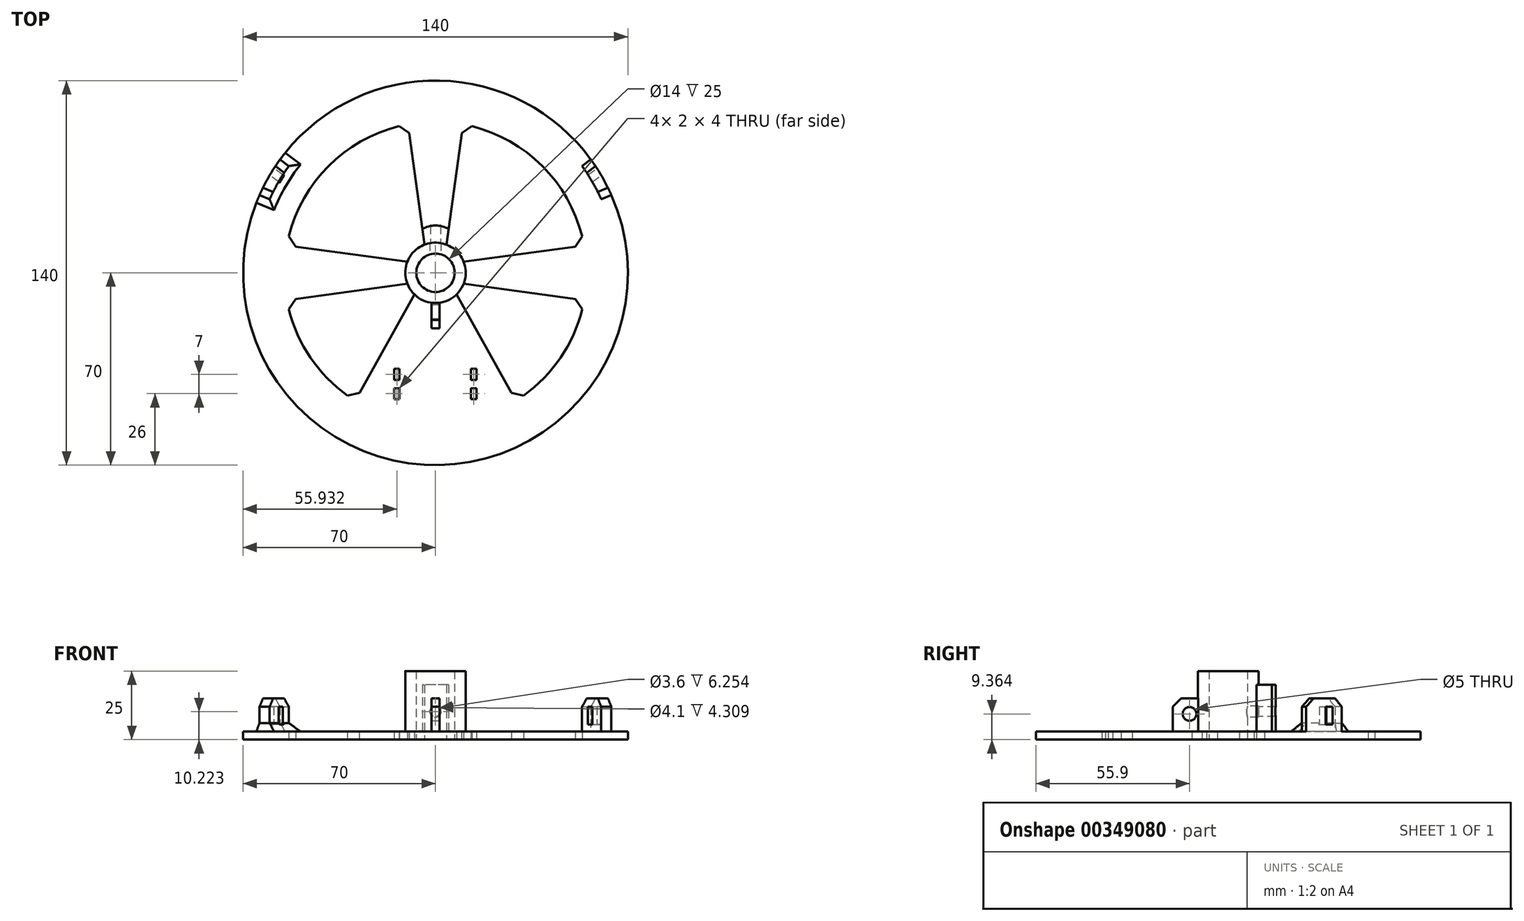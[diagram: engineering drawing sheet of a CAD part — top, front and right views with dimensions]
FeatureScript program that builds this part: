
annotation { "Feature Type Name" : "Feature", "Feature Type Description" : "" }
export const myFeature = defineFeature(function(context is Context, id is Id, definition is map)
    precondition{}
    {
        {
            var Q0;
            Q0=qCreatedBy(makeId("Top.planeOp"),FACE);
            var sketch = newSketch(context, id + "F0", { "sketchPlane" : qUnion([Q0])});
            skLineSegment(sketch, "E0", {"start": v(0, 0) * mm, "end": v(69.9, 40.35) * mm, "construction": true});
            skLineSegment(sketch, "E1", {"start": v(0, 0) * mm, "end": v(-75.47, 43.58) * mm, "construction": true});
            skLineSegment(sketch, "E2", {"start": v(0, 0) * mm, "end": v(0, -74.2) * mm, "construction": true});
            skArc(sketch, "E3", {"start": v(-56.52, 41.3) * mm, "mid": v(-60.62, 35) * mm, "end": v(-64.02, 28.3) * mm});
            skArc(sketch, "E4", {"start": v(-64.02, 28.3) * mm, "mid": v(60.62, -35) * mm, "end": v(-56.52, 41.3) * mm});
            skArc(sketch, "E5", {"start": v(-53.34, 38.88) * mm, "mid": v(-57.16, 33) * mm, "end": v(-60.34, 26.75) * mm});
            skLineSegment(sketch, "E6", {"start": v(-64.02, 28.3) * mm, "end": v(-60.34, 26.75) * mm});
            skLineSegment(sketch, "E7", {"start": v(-53.34, 38.88) * mm, "end": v(-56.52, 41.3) * mm});
            skCircle(sketch, "E8", {"center": v(0, 0) * mm, "radius": 7 * mm});
            skCircle(sketch, "E9", {"center": v(0, 0) * mm, "radius": 11 * mm});
            skArc(sketch, "E10.2.0", {"start": v(60.34, 26.75) * mm, "mid": v(57.16, 33) * mm, "end": v(53.34, 38.88) * mm});
            skArc(sketch, "E10.2.1", {"start": v(64.02, 28.3) * mm, "mid": v(60.62, 35) * mm, "end": v(56.52, 41.3) * mm});
            skLineSegment(sketch, "E10.2.2", {"start": v(56.52, 41.3) * mm, "end": v(53.34, 38.88) * mm});
            skLineSegment(sketch, "E10.2.3", {"start": v(60.34, 26.75) * mm, "end": v(64.02, 28.3) * mm});
            skCircle(sketch, "E11", {"center": v(0, 0) * mm, "radius": 55 * mm});
            skLineSegment(sketch, "E12", {"start": v(0, 71.1) * mm, "end": v(0, -3.57) * mm, "construction": true});
            skLineSegment(sketch, "E13", {"start": v(-10, 54.08) * mm, "end": v(-4, 10.25) * mm});
            skLineSegment(sketch, "E14", {"start": v(10, 54.08) * mm, "end": v(4, 10.25) * mm});
            skLineSegment(sketch, "E15.1.0", {"start": v(-54.08, 10) * mm, "end": v(-10.25, 4) * mm});
            skLineSegment(sketch, "E15.1.1", {"start": v(-54.08, -10) * mm, "end": v(-10.25, -4) * mm});
            skLineSegment(sketch, "E15.3.0", {"start": v(54.08, -10) * mm, "end": v(10.25, -4) * mm});
            skLineSegment(sketch, "E15.3.1", {"start": v(54.08, 10) * mm, "end": v(10.25, 4) * mm});
            skArc(sketch, "E16", {"start": v(4.77, 15.87) * mm, "mid": v(0, 17.25) * mm, "end": v(-4.77, 15.87) * mm});
            skLineSegment(sketch, "E17", {"start": v(-1.5, -10.9) * mm, "end": v(-1.5, -20.16) * mm});
            skLineSegment(sketch, "E18", {"start": v(-1.5, -20.16) * mm, "end": v(1.5, -20.16) * mm});
            skLineSegment(sketch, "E19", {"start": v(1.5, -20.16) * mm, "end": v(1.5, -10.9) * mm});
            skLineSegment(sketch, "E20.bottom", {"start": v(-15.07, -35) * mm, "end": v(-13.07, -35) * mm});
            skLineSegment(sketch, "E20.top", {"start": v(-15.07, -39) * mm, "end": v(-13.07, -39) * mm});
            skLineSegment(sketch, "E20.left", {"start": v(-15.07, -35) * mm, "end": v(-15.07, -39) * mm});
            skLineSegment(sketch, "E20.right", {"start": v(-13.07, -35) * mm, "end": v(-13.07, -39) * mm});
            skLineSegment(sketch, "E21.bottom", {"start": v(12.93, -35) * mm, "end": v(14.93, -35) * mm});
            skLineSegment(sketch, "E21.top", {"start": v(12.93, -39) * mm, "end": v(14.93, -39) * mm});
            skLineSegment(sketch, "E21.left", {"start": v(12.93, -35) * mm, "end": v(12.93, -39) * mm});
            skLineSegment(sketch, "E21.right", {"start": v(14.93, -35) * mm, "end": v(14.93, -39) * mm});
            skLineSegment(sketch, "E22", {"start": v(-18.61, -37) * mm, "end": v(20.4, -37) * mm, "construction": true});
            skLineSegment(sketch, "E23.bottom", {"start": v(-15.07, -42) * mm, "end": v(-13.07, -42) * mm});
            skLineSegment(sketch, "E23.top", {"start": v(-15.07, -46) * mm, "end": v(-13.07, -46) * mm});
            skLineSegment(sketch, "E23.left", {"start": v(-15.07, -42) * mm, "end": v(-15.07, -46) * mm});
            skLineSegment(sketch, "E23.right", {"start": v(-13.07, -42) * mm, "end": v(-13.07, -46) * mm});
            skLineSegment(sketch, "E24.bottom", {"start": v(12.93, -42) * mm, "end": v(14.93, -42) * mm});
            skLineSegment(sketch, "E24.top", {"start": v(12.93, -46) * mm, "end": v(14.93, -46) * mm});
            skLineSegment(sketch, "E24.left", {"start": v(12.93, -42) * mm, "end": v(12.93, -46) * mm});
            skLineSegment(sketch, "E24.right", {"start": v(14.93, -42) * mm, "end": v(14.93, -46) * mm});
            skLineSegment(sketch, "E25", {"start": v(-18.62, -44) * mm, "end": v(19.75, -44) * mm, "construction": true});
            skLineSegment(sketch, "E26", {"start": v(-14.07, -36.98) * mm, "end": v(-14.07, -57.94) * mm, "construction": true});
            skPoint(sketch, "E26.startSnap0", {"position": v(-14.07, -35) * mm});
            skLineSegment(sketch, "E27", {"start": v(-7.65, -7.9) * mm, "end": v(-29.25, -46.57) * mm});
            skLineSegment(sketch, "E28", {"start": v(7.65, -7.9) * mm, "end": v(29.25, -46.57) * mm});
            skSolve(sketch);
        }
        {
            var Q0;
            Q0=makeQuery(id+"F0.imprint","IMPRINT",FACE,{"disambiguationData":[TD([[makeQuery(id+"F0.imprint","IMPRINT",EDGE,{"derivedFrom":sQuery(id+"F0.wireOp",EDGE,"E3")}),1.0]])]});
            var Q1;
            Q1=makeQuery(id+"F0.imprint","IMPRINT",FACE,{"disambiguationData":[TD([[makeQuery(id+"F0.imprint","IMPRINT",EDGE,{"derivedFrom":sQuery(id+"F0.wireOp",EDGE,"E5")}),1.0]])]});
            var Q2;
            Q2=makeQuery(id+"F0.imprint","IMPRINT",FACE,{"disambiguationData":[TD([[makeQuery(id+"F0.imprint","IMPRINT",EDGE,{"derivedFrom":sQuery(id+"F0.wireOp",EDGE,"E4")}),1.0]])]});
            var Q3;
            {var subQ0=sQuery(id+"F0.wireOp",EDGE,"E15.1.0");Q3=makeQuery(id+"F0.imprint","IMPRINT",FACE,{"disambiguationData":[TD([[makeQuery(id+"F0.imprint","IMPRINT",EDGE,{"derivedFrom":subQ0}),-1.0]])]});}
            var Q4;
            {var subQ0=sQuery(id+"F0.wireOp",EDGE,"E13");Q4=makeQuery(id+"F0.imprint","IMPRINT",FACE,{"disambiguationData":[TD([[makeQuery(id+"F0.imprint","IMPRINT",EDGE,{"derivedFrom":subQ0}),1.0]])]});}
            var Q5;
            {var subQ0=sQuery(id+"F0.wireOp",EDGE,"E15.3.0");Q5=makeQuery(id+"F0.imprint","IMPRINT",FACE,{"disambiguationData":[TD([[makeQuery(id+"F0.imprint","IMPRINT",EDGE,{"derivedFrom":subQ0}),-1.0]])]});}
            var Q6;
            {var subQ0=sQuery(id+"F0.wireOp",EDGE,"E15.2.0");Q6=makeQuery(id+"F0.imprint","IMPRINT",FACE,{"disambiguationData":[TD([[makeQuery(id+"F0.imprint","IMPRINT",EDGE,{"derivedFrom":subQ0}),-1.0]])]});}
            var Q7;
            Q7=makeQuery(id+"F0.imprint","IMPRINT",FACE,{"disambiguationData":[TD([[makeQuery(id+"F0.imprint","IMPRINT",EDGE,{"derivedFrom":sQuery(id+"F0.wireOp",EDGE,"DxC1QGky-HRrN-gzPb-Pb88-aNf4S9f9K86J.bottom")}),1.0]])]});
            var Q8;
            {var subQ0=sQuery(id+"F0.wireOp",EDGE,"E17");Q8=makeQuery(id+"F0.imprint","IMPRINT",FACE,{"disambiguationData":[TD([[makeQuery(id+"F0.imprint","IMPRINT",EDGE,{"derivedFrom":subQ0}),-1.0]])]});}
            extrude(context, id + "F1", {"entities" : qUnion([Q0, Q1, Q2, Q3, Q4, Q5, Q6, Q7, Q8]), "depth" : 3 * mm});
        }
        {
            var Q0;
            Q0=makeQuery(id+"F0.imprint","IMPRINT",FACE,{"disambiguationData":[TD([[makeQuery(id+"F0.imprint","IMPRINT",EDGE,{"derivedFrom":sQuery(id+"F0.wireOp",EDGE,"E3")}),1.0]])]});
            var Q1;
            Q1=makeQuery(id+"F0.imprint","IMPRINT",FACE,{"disambiguationData":[TD([[makeQuery(id+"F0.imprint","IMPRINT",EDGE,{"derivedFrom":sQuery(id+"F0.wireOp",EDGE,"E10.2.0")}),-1.0]])]});
            var Q2;
            Q2=makeQuery(id+"F0.imprint","IMPRINT",FACE,{"disambiguationData":[TD([[makeQuery(id+"F0.imprint","IMPRINT",EDGE,{"derivedFrom":sQuery(id+"F0.wireOp",EDGE,"E10.1.0")}),-1.0]])]});
            var Q3;
            {var subQ0=sQuery(id+"F0.wireOp",EDGE,"E17");Q3=makeQuery(id+"F0.imprint","IMPRINT",FACE,{"disambiguationData":[TD([[makeQuery(id+"F0.imprint","IMPRINT",EDGE,{"derivedFrom":subQ0}),1.0]])]});}
            extrude(context, id + "F2", {"entities" : qUnion([Q0, Q1, Q2, Q3]), "operationType" : NewBodyOperationType.ADD, "depth" : 15 * mm});
        }
        {
            var Q0;
            Q0=qCreatedBy(makeId("Right.planeOp"),FACE);
            var sketch = newSketch(context, id + "F3", { "sketchPlane" : qUnion([Q0])});
            skLineSegment(sketch, "E29", {"start": v(0, 42.43) * mm, "end": v(0, -20.95) * mm, "construction": true});
            skSolve(sketch);
        }
        {
            var Q0;
            Q0=makeQuery(id+"F0.imprint","IMPRINT",FACE,{"disambiguationData":[TD([[makeQuery(id+"F0.imprint","IMPRINT",EDGE,{"derivedFrom":sQuery(id+"F0.wireOp",EDGE,"E8")}),-1.0]])]});
            extrude(context, id + "F4", {"entities" : qUnion([Q0]), "operationType" : NewBodyOperationType.ADD, "depth" : 25 * mm});
        }
        {
            var Q0;
            {var subQ5=sQuery(id+"F0.wireOp",EDGE,"E16");Q0=makeQuery(id+"F0.imprint","IMPRINT",FACE,{"disambiguationData":[TD([[makeQuery(id+"F0.imprint","IMPRINT",EDGE,{"derivedFrom":subQ5}),1.0]])]});}
            extrude(context, id + "F5", {"entities" : qUnion([Q0]), "operationType" : NewBodyOperationType.ADD, "depth" : 20 * mm});
        }
        {
            var Q0;
            Q0=sQuery(id+"F3.wireOp",EDGE,"E29");
            cPlane(context, id + "F6", {"entities" : qUnion([Q0]), "cplaneType" : CPlaneType.LINE_ANGLE, "offset" : 25 * mm, "angle" : 90 * degree, "width" : 150 * mm, "height" : 150 * mm});
        }
        {
            var Q0;
            Q0=qCreatedBy(id+"F6.planeOp",FACE);
            var sketch = newSketch(context, id + "F7", { "sketchPlane" : qUnion([Q0])});
            skCircle(sketch, "E30", {"center": v(0, 10.22) * mm, "radius": 1 * mm});
            skSolve(sketch);
        }
        {
            var Q0;
            Q0=sQuery(id+"F7.wireOp",VERTEX,"E30.center");
            var Q1;
            Q1=makeQuery(id+"F1.opExtrude","SWEPT_BODY",BODY,{"disambiguationData":[OSD([sQuery(id+"F0.wireOp",EDGE,"E3"),sQuery(id+"F0.wireOp",EDGE,"E4"),sQuery(id+"F0.wireOp",EDGE,"E9"),sQuery(id+"F0.wireOp",EDGE,"E10.1.0"),sQuery(id+"F0.wireOp",EDGE,"E10.1.2"),sQuery(id+"F0.wireOp",EDGE,"E10.1.3"),sQuery(id+"F0.wireOp",EDGE,"E10.2.0"),sQuery(id+"F0.wireOp",EDGE,"E10.2.2"),sQuery(id+"F0.wireOp",EDGE,"E10.2.3"),sQuery(id+"F0.wireOp",EDGE,"E11"),sQuery(id+"F0.wireOp",EDGE,"E13"),sQuery(id+"F0.wireOp",EDGE,"E14"),sQuery(id+"F0.wireOp",EDGE,"E15.1.0"),sQuery(id+"F0.wireOp",EDGE,"E15.1.1"),sQuery(id+"F0.wireOp",EDGE,"E15.3.0"),sQuery(id+"F0.wireOp",EDGE,"E15.3.1"),sQuery(id+"F0.wireOp",EDGE,"DxC1QGky-HRrN-gzPb-Pb88-aNf4S9f9K86J.bottom"),sQuery(id+"F0.wireOp",EDGE,"DxC1QGky-HRrN-gzPb-Pb88-aNf4S9f9K86J.top"),sQuery(id+"F0.wireOp",EDGE,"DxC1QGky-HRrN-gzPb-Pb88-aNf4S9f9K86J.left"),sQuery(id+"F0.wireOp",EDGE,"DxC1QGky-HRrN-gzPb-Pb88-aNf4S9f9K86J.right"),sQuery(id+"F0.wireOp",EDGE,"2d52bbff-8edd-4f97-a77e-c5ac5676539f0.MirrorCS"),sQuery(id+"F0.wireOp",EDGE,"2d52bbff-8edd-4f97-a77e-c5ac5676539f1.MirrorCS"),sQuery(id+"F0.wireOp",EDGE,"2d52bbff-8edd-4f97-a77e-c5ac5676539f3.MirrorCS"),sQuery(id+"F0.wireOp",EDGE,"2d52bbff-8edd-4f97-a77e-c5ac5676539f6.MirrorCS"),sQuery(id+"F0.wireOp",EDGE,"9be3de77-d5e6-4486-93f5-ee3b1d01e160.bottom"),sQuery(id+"F0.wireOp",EDGE,"9be3de77-d5e6-4486-93f5-ee3b1d01e160.top"),sQuery(id+"F0.wireOp",EDGE,"9be3de77-d5e6-4486-93f5-ee3b1d01e160.left"),sQuery(id+"F0.wireOp",EDGE,"9be3de77-d5e6-4486-93f5-ee3b1d01e160.right"),sQuery(id+"F0.wireOp",EDGE,"a1a42e55-1d56-4dcf-bef6-dfa0cd09f213.MirrorCS"),sQuery(id+"F0.wireOp",EDGE,"69599f0c-71d3-4e93-93c2-72b703701d98.MirrorCS"),sQuery(id+"F0.wireOp",EDGE,"1db623de-f78b-4af5-8506-0e3137d38347.MirrorCS"),sQuery(id+"F0.wireOp",EDGE,"2d571f0c-88a3-41e3-b531-1a1a6e09f5e6.MirrorCS"),sQuery(id+"F0.wireOp",EDGE,"QAUAg4Rv-rJLO-vGMV-bjQP-bpTTJf4zCCb9"),sQuery(id+"F0.wireOp",EDGE,"6e9785c6-ce13-4db9-ba87-197f2c4649aa0.MirrorCS")])]});
            hole(context, id + "F8", {"style" : HoleStyle.C_BORE, "endStyle" : HoleEndStyle.THROUGH, "oppositeDirection" : true, "holeDiameter" : 3.6 * mm, "cBoreDiameter" : 4.1 * mm, "cBoreDepth" : 11 * mm, "isTappedThrough" : true, "tappedDepth" : 12 * mm, "tapClearance" : 3, "startFromSketch" : true, "locations" : qUnion([Q0]), "scope" : qUnion([Q1])});
        }
        {
            var Q0;
            Q0=makeQuery(id+"F2.opExtrude","SWEPT_EDGE",EDGE,{"disambiguationData":[OSD([sQuery(id+"F0.wireOp",EDGE,"E3"),sQuery(id+"F0.wireOp",EDGE,"E4"),sQuery(id+"F0.wireOp",EDGE,"E7")])]});
            cPlane(context, id + "F9", {"entities" : qUnion([Q0]), "cplaneType" : CPlaneType.LINE_ANGLE, "offset" : 25 * mm, "angle" : 35 * degree, "width" : 150 * mm, "height" : 150 * mm});
        }
        {
            var Q0;
            Q0=qCreatedBy(id+"F9.planeOp",FACE);
            var sketch = newSketch(context, id + "F10", { "sketchPlane" : qUnion([Q0])});
            skLineSegment(sketch, "E31.0", {"start": v(-1.4, 15) * mm, "end": v(-1.4, 3) * mm});
            skLineSegment(sketch, "E31.1", {"start": v(-1.4, 15) * mm, "end": v(13.54, 15) * mm});
            skLineSegment(sketch, "E32.bottom", {"start": v(2.6, 5.5) * mm, "end": v(5.6, 5.5) * mm});
            skLineSegment(sketch, "E32.top", {"start": v(2.6, 12) * mm, "end": v(5.6, 12) * mm});
            skLineSegment(sketch, "E32.left", {"start": v(2.6, 5.5) * mm, "end": v(2.6, 12) * mm});
            skLineSegment(sketch, "E32.right", {"start": v(5.6, 5.5) * mm, "end": v(5.6, 12) * mm});
            skSolve(sketch);
        }
        {
            var Q0;
            Q0=makeQuery(id+"F10.imprint","IMPRINT",FACE,{"disambiguationData":[TD([[makeQuery(id+"F10.imprint","IMPRINT",EDGE,{"derivedFrom":sQuery(id+"F10.wireOp",EDGE,"E32.bottom")}),1.0]])]});
            extrude(context, id + "F11", {"entities" : qUnion([Q0]), "operationType" : NewBodyOperationType.REMOVE, "oppositeDirection" : true, "depth" : 25 * mm});
        }
        {
            var Q0;
            Q0=makeQuery(id+"F2.opExtrude","SWEPT_EDGE",EDGE,{"disambiguationData":[OSD([sQuery(id+"F0.wireOp",EDGE,"E4"),sQuery(id+"F0.wireOp",EDGE,"E10.2.1"),sQuery(id+"F0.wireOp",EDGE,"E10.2.2")])]});
            cPlane(context, id + "F12", {"entities" : qUnion([Q0]), "cplaneType" : CPlaneType.LINE_ANGLE, "offset" : 25 * mm, "angle" : 35 * degree, "oppositeDirection" : true, "width" : 150 * mm, "height" : 150 * mm});
        }
        {
            var Q0;
            Q0=qCreatedBy(id+"F12.planeOp",FACE);
            var sketch = newSketch(context, id + "F13", { "sketchPlane" : qUnion([Q0])});
            skLineSegment(sketch, "E33.bottom", {"start": v(2.6, 12) * mm, "end": v(5.6, 12) * mm});
            skLineSegment(sketch, "E33.top", {"start": v(2.6, 5.5) * mm, "end": v(5.6, 5.5) * mm});
            skLineSegment(sketch, "E33.left", {"start": v(2.6, 12) * mm, "end": v(2.6, 5.5) * mm});
            skLineSegment(sketch, "E33.right", {"start": v(5.6, 12) * mm, "end": v(5.6, 5.5) * mm});
            skLineSegment(sketch, "E34.0", {"start": v(13.54, 15) * mm, "end": v(-1.4, 15) * mm});
            skSolve(sketch);
        }
        {
            var Q0;
            Q0=makeQuery(id+"F13.imprint","IMPRINT",FACE,{"disambiguationData":[TD([[makeQuery(id+"F13.imprint","IMPRINT",EDGE,{"derivedFrom":sQuery(id+"F13.wireOp",EDGE,"E33.bottom")}),-1.0]])]});
            extrude(context, id + "F14", {"entities" : qUnion([Q0]), "operationType" : NewBodyOperationType.REMOVE, "depth" : 25 * mm});
        }
        {
            var Q0;
            Q0=makeQuery(id+"F1.opExtrude","SWEPT_EDGE",EDGE,{"disambiguationData":[OSD([sQuery(id+"F0.wireOp",EDGE,"E11"),sQuery(id+"F0.wireOp",EDGE,"E13")])]});
            var Q1;
            Q1=makeQuery(id+"F1.opExtrude","SWEPT_EDGE",EDGE,{"disambiguationData":[OSD([sQuery(id+"F0.wireOp",EDGE,"E11"),sQuery(id+"F0.wireOp",EDGE,"E14")])]});
            var Q2;
            Q2=makeQuery(id+"F1.opExtrude","CAP_EDGE",EDGE,{"disambiguationData":[OSD([sQuery(id+"F0.wireOp",EDGE,"E10.2.0")])],"isStart":false});
            var Q3;
            Q3=makeQuery(id+"F2.boolean.opBoolean","INTERSECT",EDGE,{"derivedFrom":[makeQuery(id+"F1.opExtrude","CAP_FACE",FACE,{"disambiguationData":[OSD([sQuery(id+"F0.wireOp",EDGE,"E3"),sQuery(id+"F0.wireOp",EDGE,"E4"),sQuery(id+"F0.wireOp",EDGE,"E9"),sQuery(id+"F0.wireOp",EDGE,"E10.1.0"),sQuery(id+"F0.wireOp",EDGE,"E10.1.2"),sQuery(id+"F0.wireOp",EDGE,"E10.1.3"),sQuery(id+"F0.wireOp",EDGE,"E10.2.0"),sQuery(id+"F0.wireOp",EDGE,"E10.2.2"),sQuery(id+"F0.wireOp",EDGE,"E10.2.3"),sQuery(id+"F0.wireOp",EDGE,"E11"),sQuery(id+"F0.wireOp",EDGE,"E13"),sQuery(id+"F0.wireOp",EDGE,"E14"),sQuery(id+"F0.wireOp",EDGE,"E15.1.0"),sQuery(id+"F0.wireOp",EDGE,"E15.1.1"),sQuery(id+"F0.wireOp",EDGE,"E15.3.0"),sQuery(id+"F0.wireOp",EDGE,"E15.3.1"),sQuery(id+"F0.wireOp",EDGE,"DxC1QGky-HRrN-gzPb-Pb88-aNf4S9f9K86J.bottom"),sQuery(id+"F0.wireOp",EDGE,"DxC1QGky-HRrN-gzPb-Pb88-aNf4S9f9K86J.top"),sQuery(id+"F0.wireOp",EDGE,"DxC1QGky-HRrN-gzPb-Pb88-aNf4S9f9K86J.left"),sQuery(id+"F0.wireOp",EDGE,"DxC1QGky-HRrN-gzPb-Pb88-aNf4S9f9K86J.right"),sQuery(id+"F0.wireOp",EDGE,"2d52bbff-8edd-4f97-a77e-c5ac5676539f0.MirrorCS"),sQuery(id+"F0.wireOp",EDGE,"2d52bbff-8edd-4f97-a77e-c5ac5676539f1.MirrorCS"),sQuery(id+"F0.wireOp",EDGE,"2d52bbff-8edd-4f97-a77e-c5ac5676539f3.MirrorCS"),sQuery(id+"F0.wireOp",EDGE,"2d52bbff-8edd-4f97-a77e-c5ac5676539f6.MirrorCS"),sQuery(id+"F0.wireOp",EDGE,"9be3de77-d5e6-4486-93f5-ee3b1d01e160.bottom"),sQuery(id+"F0.wireOp",EDGE,"9be3de77-d5e6-4486-93f5-ee3b1d01e160.top"),sQuery(id+"F0.wireOp",EDGE,"9be3de77-d5e6-4486-93f5-ee3b1d01e160.left"),sQuery(id+"F0.wireOp",EDGE,"9be3de77-d5e6-4486-93f5-ee3b1d01e160.right"),sQuery(id+"F0.wireOp",EDGE,"a1a42e55-1d56-4dcf-bef6-dfa0cd09f213.MirrorCS"),sQuery(id+"F0.wireOp",EDGE,"69599f0c-71d3-4e93-93c2-72b703701d98.MirrorCS"),sQuery(id+"F0.wireOp",EDGE,"1db623de-f78b-4af5-8506-0e3137d38347.MirrorCS"),sQuery(id+"F0.wireOp",EDGE,"2d571f0c-88a3-41e3-b531-1a1a6e09f5e6.MirrorCS"),sQuery(id+"F0.wireOp",EDGE,"QAUAg4Rv-rJLO-vGMV-bjQP-bpTTJf4zCCb9"),sQuery(id+"F0.wireOp",EDGE,"6e9785c6-ce13-4db9-ba87-197f2c4649aa0.MirrorCS")])],"isStart":false}),makeQuery(id+"F2.opExtrude","SWEPT_FACE",FACE,{"disambiguationData":[OSD([sQuery(id+"F0.wireOp",EDGE,"E5")])]})]});
            var Q4;
            {var subQ0=sQuery(id+"F0.wireOp",EDGE,"E13");var subQ1=sQuery(id+"F0.wireOp",EDGE,"E9");Q4=makeQuery(id+"F5.boolean.opBoolean","MERGE",EDGE,{"derivedFrom":[makeQuery(id+"F1.opExtrude","SWEPT_EDGE",EDGE,{"disambiguationData":[OSD([subQ1,subQ0])]}),makeQuery(id+"F5.opExtrude","SWEPT_EDGE",EDGE,{"disambiguationData":[OSD([subQ1,subQ0])]})]});}
            var Q5;
            {var subQ0=sQuery(id+"F0.wireOp",EDGE,"E14");var subQ1=sQuery(id+"F0.wireOp",EDGE,"E9");Q5=makeQuery(id+"F5.boolean.opBoolean","MERGE",EDGE,{"derivedFrom":[makeQuery(id+"F1.opExtrude","SWEPT_EDGE",EDGE,{"disambiguationData":[OSD([subQ1,subQ0])]}),makeQuery(id+"F5.opExtrude","SWEPT_EDGE",EDGE,{"disambiguationData":[OSD([subQ1,subQ0])]})]});}
            var Q6;
            Q6=makeQuery(id+"F1.opExtrude","SWEPT_EDGE",EDGE,{"disambiguationData":[OSD([sQuery(id+"F0.wireOp",EDGE,"E9"),sQuery(id+"F0.wireOp",EDGE,"E15.1.0")])]});
            var Q7;
            Q7=makeQuery(id+"F1.opExtrude","SWEPT_EDGE",EDGE,{"disambiguationData":[OSD([sQuery(id+"F0.wireOp",EDGE,"E11"),sQuery(id+"F0.wireOp",EDGE,"E15.1.0")])]});
            var Q8;
            Q8=makeQuery(id+"F1.opExtrude","SWEPT_EDGE",EDGE,{"disambiguationData":[OSD([sQuery(id+"F0.wireOp",EDGE,"E9"),sQuery(id+"F0.wireOp",EDGE,"E15.3.1")])]});
            var Q9;
            Q9=makeQuery(id+"F1.opExtrude","SWEPT_EDGE",EDGE,{"disambiguationData":[OSD([sQuery(id+"F0.wireOp",EDGE,"E11"),sQuery(id+"F0.wireOp",EDGE,"E15.3.1")])]});
            var Q10;
            Q10=makeQuery(id+"F1.opExtrude","SWEPT_EDGE",EDGE,{"disambiguationData":[OSD([sQuery(id+"F0.wireOp",EDGE,"E11"),sQuery(id+"F0.wireOp",EDGE,"E15.1.1")])]});
            var Q11;
            Q11=makeQuery(id+"F1.opExtrude","SWEPT_EDGE",EDGE,{"disambiguationData":[OSD([sQuery(id+"F0.wireOp",EDGE,"E15.3.0"),sQuery(id+"F0.wireOp",EDGE,"6e9785c6-ce13-4db9-ba87-197f2c4649aa0.MirrorCS")])]});
            var Q12;
            Q12=makeQuery(id+"F1.opExtrude","SWEPT_EDGE",EDGE,{"disambiguationData":[OSD([sQuery(id+"F0.wireOp",EDGE,"E11"),sQuery(id+"F0.wireOp",EDGE,"E15.3.0")])]});
            var Q13;
            Q13=makeQuery(id+"F1.opExtrude","SWEPT_EDGE",EDGE,{"disambiguationData":[OSD([sQuery(id+"F0.wireOp",EDGE,"E15.1.1"),sQuery(id+"F0.wireOp",EDGE,"QAUAg4Rv-rJLO-vGMV-bjQP-bpTTJf4zCCb9")])]});
            var Q14;
            Q14=makeQuery(id+"F1.opExtrude","SWEPT_EDGE",EDGE,{"disambiguationData":[OSD([sQuery(id+"F0.wireOp",EDGE,"E11"),sQuery(id+"F0.wireOp",EDGE,"QAUAg4Rv-rJLO-vGMV-bjQP-bpTTJf4zCCb9")])]});
            var Q15;
            Q15=makeQuery(id+"F1.opExtrude","SWEPT_EDGE",EDGE,{"disambiguationData":[OSD([sQuery(id+"F0.wireOp",EDGE,"E11"),sQuery(id+"F0.wireOp",EDGE,"6e9785c6-ce13-4db9-ba87-197f2c4649aa0.MirrorCS")])]});
            var Q16;
            Q16=makeQuery(id+"F1.opExtrude","CAP_EDGE",EDGE,{"disambiguationData":[OSD([sQuery(id+"F0.wireOp",EDGE,"E10.1.0")])],"isStart":false});
            var Q17;
            {var subQ0=sQuery(id+"F0.wireOp",EDGE,"E9");var subQ1=makeQuery(id+"F0.imprint","INTERSECT",VERTEX,{"derivedFrom":[subQ0,sQuery(id+"F0.wireOp",EDGE,"E15.3.0")]});var subQ2=makeQuery(id+"F0.imprint","INTERSECT",VERTEX,{"derivedFrom":[subQ0,sQuery(id+"F0.wireOp",EDGE,"E15.1.1")]});Q17=makeQuery(id+"F1.opExtrude","CAP_EDGE",EDGE,{"disambiguationData":[OSD([subQ0]),TDD([makeQuery(id+"F0.imprint","IMPRINT",EDGE,{"disambiguationData":[TD([[makeQuery(id+"F0.imprint","INTERSECT",VERTEX,{"derivedFrom":[subQ0,sQuery(id+"F0.wireOp",EDGE,"E15.1.0")]}),-1.0]])],"derivedFrom":subQ0}),makeQuery(id+"F0.imprint","IMPRINT",EDGE,{"disambiguationData":[TD([[subQ2,-1.0]])],"derivedFrom":subQ0}),makeQuery(id+"F0.imprint","IMPRINT",EDGE,{"disambiguationData":[TD([[subQ1,-1.0]])],"derivedFrom":subQ0})])],"isStart":false});}
            var Q18;
            {var subQ0=sQuery(id+"F0.wireOp",EDGE,"E9");Q18=makeQuery(id+"F1.opExtrude","CAP_EDGE",EDGE,{"disambiguationData":[OSD([subQ0]),TDD([makeQuery(id+"F0.imprint","IMPRINT",EDGE,{"disambiguationData":[TD([[makeQuery(id+"F0.imprint","INTERSECT",VERTEX,{"derivedFrom":[subQ0,sQuery(id+"F0.wireOp",EDGE,"E17")]}),1.0]])],"derivedFrom":subQ0})])],"isStart":false});}
            var Q19;
            {var subQ0=sQuery(id+"F0.wireOp",EDGE,"E9");Q19=makeQuery(id+"F1.opExtrude","CAP_EDGE",EDGE,{"disambiguationData":[OSD([subQ0]),TDD([makeQuery(id+"F0.imprint","IMPRINT",EDGE,{"disambiguationData":[TD([[makeQuery(id+"F0.imprint","INTERSECT",VERTEX,{"derivedFrom":[subQ0,sQuery(id+"F0.wireOp",EDGE,"E19")]}),-1.0]])],"derivedFrom":subQ0})])],"isStart":false});}
            var Q20;
            Q20=makeQuery(id+"F1.opExtrude","CAP_EDGE",EDGE,{"disambiguationData":[OSD([sQuery(id+"F0.wireOp",EDGE,"E17")])],"isStart":false});
            var Q21;
            Q21=makeQuery(id+"F1.opExtrude","CAP_EDGE",EDGE,{"disambiguationData":[OSD([sQuery(id+"F0.wireOp",EDGE,"E19")])],"isStart":false});
            var Q22;
            Q22=makeQuery(id+"F1.opExtrude","CAP_EDGE",EDGE,{"disambiguationData":[OSD([sQuery(id+"F0.wireOp",EDGE,"E18")])],"isStart":false});
            var Q23;
            Q23=makeQuery(id+"F2.opExtrude","CAP_EDGE",EDGE,{"disambiguationData":[OSD([sQuery(id+"F0.wireOp",EDGE,"E18")])],"isStart":false});
            var Q24;
            Q24=makeQuery(id+"F2.opExtrude","CAP_EDGE",EDGE,{"disambiguationData":[OSD([sQuery(id+"F0.wireOp",EDGE,"E6")])],"isStart":false});
            var Q25;
            Q25=makeQuery(id+"F2.opExtrude","CAP_EDGE",EDGE,{"disambiguationData":[OSD([sQuery(id+"F0.wireOp",EDGE,"E10.2.3")])],"isStart":false});
            var Q26;
            Q26=makeQuery(id+"F2.opExtrude","CAP_EDGE",EDGE,{"disambiguationData":[OSD([sQuery(id+"F0.wireOp",EDGE,"E10.2.2")])],"isStart":false});
            var Q27;
            Q27=makeQuery(id+"F2.opExtrude","CAP_EDGE",EDGE,{"disambiguationData":[OSD([sQuery(id+"F0.wireOp",EDGE,"E7")])],"isStart":false});
            var Q28;
            Q28=makeQuery(id+"F1.opExtrude","SWEPT_EDGE",EDGE,{"disambiguationData":[OSD([sQuery(id+"F0.wireOp",EDGE,"E9"),sQuery(id+"F0.wireOp",EDGE,"E28")])]});
            var Q29;
            Q29=makeQuery(id+"F1.opExtrude","SWEPT_EDGE",EDGE,{"disambiguationData":[OSD([sQuery(id+"F0.wireOp",EDGE,"E9"),sQuery(id+"F0.wireOp",EDGE,"E27")])]});
            var Q30;
            Q30=makeQuery(id+"F1.opExtrude","CAP_EDGE",EDGE,{"disambiguationData":[OSD([sQuery(id+"F0.wireOp",EDGE,"E10.2.3")])],"isStart":false});
            var Q31;
            Q31=makeQuery(id+"F2.boolean.opBoolean","INTERSECT",EDGE,{"derivedFrom":[makeQuery(id+"F1.opExtrude","CAP_FACE",FACE,{"disambiguationData":[OSD([sQuery(id+"F0.wireOp",EDGE,"E3"),sQuery(id+"F0.wireOp",EDGE,"E4"),sQuery(id+"F0.wireOp",EDGE,"E9"),sQuery(id+"F0.wireOp",EDGE,"E10.2.0"),sQuery(id+"F0.wireOp",EDGE,"E10.2.2"),sQuery(id+"F0.wireOp",EDGE,"E10.2.3"),sQuery(id+"F0.wireOp",EDGE,"E11"),sQuery(id+"F0.wireOp",EDGE,"E13"),sQuery(id+"F0.wireOp",EDGE,"E14"),sQuery(id+"F0.wireOp",EDGE,"E15.1.0"),sQuery(id+"F0.wireOp",EDGE,"E15.1.1"),sQuery(id+"F0.wireOp",EDGE,"E15.3.0"),sQuery(id+"F0.wireOp",EDGE,"E15.3.1"),sQuery(id+"F0.wireOp",EDGE,"E17"),sQuery(id+"F0.wireOp",EDGE,"E18"),sQuery(id+"F0.wireOp",EDGE,"E19"),sQuery(id+"F0.wireOp",EDGE,"E20.bottom"),sQuery(id+"F0.wireOp",EDGE,"E20.top"),sQuery(id+"F0.wireOp",EDGE,"E20.left"),sQuery(id+"F0.wireOp",EDGE,"E20.right"),sQuery(id+"F0.wireOp",EDGE,"E21.bottom"),sQuery(id+"F0.wireOp",EDGE,"E21.top"),sQuery(id+"F0.wireOp",EDGE,"E21.left"),sQuery(id+"F0.wireOp",EDGE,"E21.right"),sQuery(id+"F0.wireOp",EDGE,"E23.bottom"),sQuery(id+"F0.wireOp",EDGE,"E23.top"),sQuery(id+"F0.wireOp",EDGE,"E23.left"),sQuery(id+"F0.wireOp",EDGE,"E23.right"),sQuery(id+"F0.wireOp",EDGE,"E24.bottom"),sQuery(id+"F0.wireOp",EDGE,"E24.top"),sQuery(id+"F0.wireOp",EDGE,"E24.left"),sQuery(id+"F0.wireOp",EDGE,"E24.right"),sQuery(id+"F0.wireOp",EDGE,"E27"),sQuery(id+"F0.wireOp",EDGE,"E28")])],"isStart":false}),makeQuery(id+"F2.opExtrude","SWEPT_FACE",FACE,{"disambiguationData":[OSD([sQuery(id+"F0.wireOp",EDGE,"E6")])]})]});
            var Q32;
            Q32=makeQuery(id+"F1.opExtrude","CAP_EDGE",EDGE,{"disambiguationData":[OSD([sQuery(id+"F0.wireOp",EDGE,"E10.2.2")])],"isStart":false});
            var Q33;
            Q33=makeQuery(id+"F2.boolean.opBoolean","INTERSECT",EDGE,{"derivedFrom":[makeQuery(id+"F1.opExtrude","CAP_FACE",FACE,{"disambiguationData":[OSD([sQuery(id+"F0.wireOp",EDGE,"E3"),sQuery(id+"F0.wireOp",EDGE,"E4"),sQuery(id+"F0.wireOp",EDGE,"E9"),sQuery(id+"F0.wireOp",EDGE,"E10.2.0"),sQuery(id+"F0.wireOp",EDGE,"E10.2.2"),sQuery(id+"F0.wireOp",EDGE,"E10.2.3"),sQuery(id+"F0.wireOp",EDGE,"E11"),sQuery(id+"F0.wireOp",EDGE,"E13"),sQuery(id+"F0.wireOp",EDGE,"E14"),sQuery(id+"F0.wireOp",EDGE,"E15.1.0"),sQuery(id+"F0.wireOp",EDGE,"E15.1.1"),sQuery(id+"F0.wireOp",EDGE,"E15.3.0"),sQuery(id+"F0.wireOp",EDGE,"E15.3.1"),sQuery(id+"F0.wireOp",EDGE,"E17"),sQuery(id+"F0.wireOp",EDGE,"E18"),sQuery(id+"F0.wireOp",EDGE,"E19"),sQuery(id+"F0.wireOp",EDGE,"E20.bottom"),sQuery(id+"F0.wireOp",EDGE,"E20.top"),sQuery(id+"F0.wireOp",EDGE,"E20.left"),sQuery(id+"F0.wireOp",EDGE,"E20.right"),sQuery(id+"F0.wireOp",EDGE,"E21.bottom"),sQuery(id+"F0.wireOp",EDGE,"E21.top"),sQuery(id+"F0.wireOp",EDGE,"E21.left"),sQuery(id+"F0.wireOp",EDGE,"E21.right"),sQuery(id+"F0.wireOp",EDGE,"E23.bottom"),sQuery(id+"F0.wireOp",EDGE,"E23.top"),sQuery(id+"F0.wireOp",EDGE,"E23.left"),sQuery(id+"F0.wireOp",EDGE,"E23.right"),sQuery(id+"F0.wireOp",EDGE,"E24.bottom"),sQuery(id+"F0.wireOp",EDGE,"E24.top"),sQuery(id+"F0.wireOp",EDGE,"E24.left"),sQuery(id+"F0.wireOp",EDGE,"E24.right"),sQuery(id+"F0.wireOp",EDGE,"E27"),sQuery(id+"F0.wireOp",EDGE,"E28")])],"isStart":false}),makeQuery(id+"F2.opExtrude","SWEPT_FACE",FACE,{"disambiguationData":[OSD([sQuery(id+"F0.wireOp",EDGE,"E7")])]})]});
            chamfer(context, id + "F15", {"entities" : qUnion([Q0, Q1, Q2, Q3, Q4, Q5, Q6, Q7, Q8, Q9, Q10, Q11, Q12, Q13, Q14, Q15, Q16, Q17, Q18, Q19, Q20, Q21, Q22, Q23, Q24, Q25, Q26, Q27, Q28, Q29, Q30, Q31, Q32, Q33]), "width" : 3 * mm, "tangentPropagation" : true});
        }
        {
            var Q0;
            Q0=makeQuery(id+"F2.opExtrude","SWEPT_FACE",FACE,{"disambiguationData":[OSD([sQuery(id+"F0.wireOp",EDGE,"E19")])]});
            var sketch = newSketch(context, id + "F16", { "sketchPlane" : qUnion([Q0])});
            skLineSegment(sketch, "E35", {"start": v(-14.1, 17.78) * mm, "end": v(-14.1, -3.48) * mm, "construction": true});
            skPoint(sketch, "E35.startSnap0", {"position": v(-14.1, 15) * mm});
            skCircle(sketch, "E36", {"center": v(-14.1, 9.36) * mm, "radius": 2.5 * mm});
            skSolve(sketch);
        }
        {
            var Q0;
            Q0 = qSketchRegion(id + "F16", true);
            extrude(context, id + "F17", {"entities" : qUnion([Q0]), "operationType" : NewBodyOperationType.REMOVE, "oppositeDirection" : true, "depth" : 25 * mm});
        }
    });
